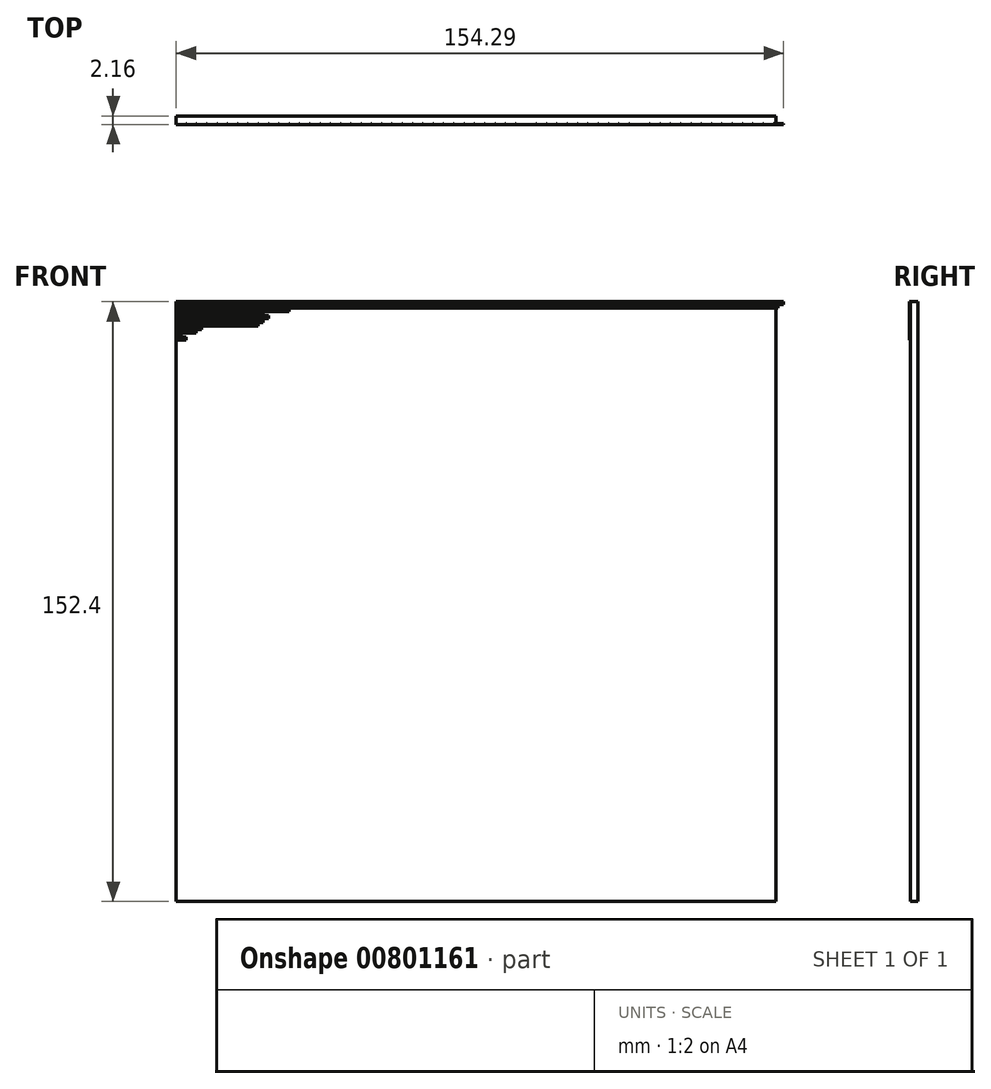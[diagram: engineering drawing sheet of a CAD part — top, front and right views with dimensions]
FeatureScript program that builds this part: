
annotation { "Feature Type Name" : "Feature", "Feature Type Description" : "" }
export const myFeature = defineFeature(function(context is Context, id is Id, definition is map)
    precondition{}
    {
        {
            var Q0;
            Q0=qCreatedBy(makeId("Front.planeOp"),FACE);
            var sketch = newSketch(context, id + "F0", { "sketchPlane" : qUnion([Q0])});
            skLineSegment(sketch, "E0.bottom", {"start": v(-76.2, -76.2) * mm, "end": v(76.2, -76.2) * mm});
            skLineSegment(sketch, "E0.top", {"start": v(-76.2, 76.2) * mm, "end": v(76.2, 76.2) * mm});
            skLineSegment(sketch, "E0.left", {"start": v(-76.2, -76.2) * mm, "end": v(-76.2, 76.2) * mm});
            skLineSegment(sketch, "E0.right", {"start": v(76.2, -76.2) * mm, "end": v(76.2, 76.2) * mm});
            skPoint(sketch, "E0.middle", {"position": v(0, 0) * mm});
            skSolve(sketch);
        }
        {
            var Q0;
            Q0 = qSketchRegion(id + "F0", true);
            extrude(context, id + "F1", {"entities" : qUnion([Q0]), "depth" : 1.9 * mm, "offsetDistance" : 25.4 * mm});
        }
        {
            var Q0;
            Q0=makeQuery(id+"F1.opExtrude","CAP_FACE",FACE,{"disambiguationData":[OSD([sQuery(id+"F0.wireOp",EDGE,"E0.bottom"),sQuery(id+"F0.wireOp",EDGE,"E0.top"),sQuery(id+"F0.wireOp",EDGE,"E0.left"),sQuery(id+"F0.wireOp",EDGE,"E0.right")])],"isStart":false});
            var sketch = newSketch(context, id + "F2", { "sketchPlane" : qUnion([Q0])});
            skLineSegment(sketch, "E1.bottom", {"start": v(-76.2, 76.2) * mm, "end": v(-73.71, 76.2) * mm});
            skLineSegment(sketch, "E1.top", {"start": v(-76.2, 75.44) * mm, "end": v(-73.71, 75.44) * mm});
            skLineSegment(sketch, "E1.left", {"start": v(-76.2, 76.2) * mm, "end": v(-76.2, 75.44) * mm});
            skLineSegment(sketch, "E1.right", {"start": v(-73.71, 76.2) * mm, "end": v(-73.71, 75.44) * mm});
            skLineSegment(sketch, "E2.bottom", {"start": v(-73.58, 76.2) * mm, "end": v(-71.1, 76.2) * mm});
            skLineSegment(sketch, "E2.top", {"start": v(-73.58, 75.44) * mm, "end": v(-71.1, 75.44) * mm});
            skLineSegment(sketch, "E2.left", {"start": v(-73.58, 76.2) * mm, "end": v(-73.58, 75.44) * mm});
            skLineSegment(sketch, "E2.right", {"start": v(-71.1, 76.2) * mm, "end": v(-71.1, 75.44) * mm});
            skLineSegment(sketch, "E3.bottom", {"start": v(-70.99, 76.2) * mm, "end": v(-68.49, 76.2) * mm});
            skLineSegment(sketch, "E3.top", {"start": v(-70.99, 75.44) * mm, "end": v(-68.49, 75.44) * mm});
            skLineSegment(sketch, "E3.left", {"start": v(-70.99, 76.2) * mm, "end": v(-70.99, 75.44) * mm});
            skLineSegment(sketch, "E3.right", {"start": v(-68.49, 76.2) * mm, "end": v(-68.49, 75.44) * mm});
            skLineSegment(sketch, "E4.bottom", {"start": v(-68.35, 76.2) * mm, "end": v(-65.86, 76.2) * mm});
            skLineSegment(sketch, "E4.top", {"start": v(-68.35, 75.44) * mm, "end": v(-65.86, 75.44) * mm});
            skLineSegment(sketch, "E4.left", {"start": v(-68.35, 76.2) * mm, "end": v(-68.35, 75.44) * mm});
            skLineSegment(sketch, "E4.right", {"start": v(-65.86, 76.2) * mm, "end": v(-65.86, 75.44) * mm});
            skLineSegment(sketch, "E5.bottom", {"start": v(-65.72, 76.2) * mm, "end": v(-63.23, 76.2) * mm});
            skLineSegment(sketch, "E5.top", {"start": v(-65.72, 75.44) * mm, "end": v(-63.23, 75.44) * mm});
            skLineSegment(sketch, "E5.left", {"start": v(-65.72, 76.2) * mm, "end": v(-65.72, 75.44) * mm});
            skLineSegment(sketch, "E5.right", {"start": v(-63.23, 76.2) * mm, "end": v(-63.23, 75.44) * mm});
            skLineSegment(sketch, "E6.bottom", {"start": v(-63.1, 76.2) * mm, "end": v(-60.62, 76.2) * mm});
            skLineSegment(sketch, "E6.top", {"start": v(-63.1, 75.44) * mm, "end": v(-60.62, 75.44) * mm});
            skLineSegment(sketch, "E6.left", {"start": v(-63.1, 76.2) * mm, "end": v(-63.1, 75.44) * mm});
            skLineSegment(sketch, "E6.right", {"start": v(-60.62, 76.2) * mm, "end": v(-60.62, 75.44) * mm});
            skLineSegment(sketch, "E7.bottom", {"start": v(-60.5, 76.2) * mm, "end": v(-58.02, 76.2) * mm});
            skLineSegment(sketch, "E7.top", {"start": v(-60.5, 75.44) * mm, "end": v(-58.02, 75.44) * mm});
            skLineSegment(sketch, "E7.left", {"start": v(-60.5, 76.2) * mm, "end": v(-60.5, 75.44) * mm});
            skLineSegment(sketch, "E7.right", {"start": v(-58.02, 76.2) * mm, "end": v(-58.02, 75.44) * mm});
            skLineSegment(sketch, "E8.bottom", {"start": v(-57.9, 76.2) * mm, "end": v(-55.4, 76.2) * mm});
            skLineSegment(sketch, "E8.top", {"start": v(-57.9, 75.44) * mm, "end": v(-55.4, 75.44) * mm});
            skLineSegment(sketch, "E8.left", {"start": v(-57.9, 76.2) * mm, "end": v(-57.9, 75.44) * mm});
            skLineSegment(sketch, "E8.right", {"start": v(-55.4, 76.2) * mm, "end": v(-55.4, 75.44) * mm});
            skLineSegment(sketch, "E9.bottom", {"start": v(-55.27, 76.2) * mm, "end": v(-52.78, 76.2) * mm});
            skLineSegment(sketch, "E9.top", {"start": v(-55.27, 75.44) * mm, "end": v(-52.78, 75.44) * mm});
            skLineSegment(sketch, "E9.left", {"start": v(-55.27, 76.2) * mm, "end": v(-55.27, 75.44) * mm});
            skLineSegment(sketch, "E9.right", {"start": v(-52.78, 76.2) * mm, "end": v(-52.78, 75.44) * mm});
            skPoint(sketch, "E10.oppositeSnap0", {"position": v(-74.96, 75.44) * mm});
            skLineSegment(sketch, "E10.bottom", {"start": v(-76.2, 75.44) * mm, "end": v(-74.96, 75.44) * mm});
            skLineSegment(sketch, "E10.left", {"start": v(-76.2, 75.44) * mm, "end": v(-76.2, 75.32) * mm});
            skLineSegment(sketch, "E11.bottom", {"start": v(-76.2, 75.32) * mm, "end": v(-75.01, 75.32) * mm});
            skLineSegment(sketch, "E11.top", {"start": v(-76.2, 74.56) * mm, "end": v(-75.01, 74.56) * mm});
            skLineSegment(sketch, "E11.left", {"start": v(-76.2, 75.32) * mm, "end": v(-76.2, 74.56) * mm});
            skLineSegment(sketch, "E11.right", {"start": v(-75.01, 75.32) * mm, "end": v(-75.01, 74.56) * mm});
            skLineSegment(sketch, "E12.bottom", {"start": v(-74.88, 75.32) * mm, "end": v(-72.38, 75.32) * mm});
            skLineSegment(sketch, "E12.top", {"start": v(-74.88, 74.56) * mm, "end": v(-72.38, 74.56) * mm});
            skLineSegment(sketch, "E12.left", {"start": v(-74.88, 75.32) * mm, "end": v(-74.88, 74.56) * mm});
            skLineSegment(sketch, "E12.right", {"start": v(-72.38, 75.32) * mm, "end": v(-72.38, 74.56) * mm});
            skLineSegment(sketch, "E13.bottom", {"start": v(-72.26, 75.32) * mm, "end": v(-69.76, 75.32) * mm});
            skLineSegment(sketch, "E13.top", {"start": v(-72.26, 74.56) * mm, "end": v(-69.76, 74.56) * mm});
            skLineSegment(sketch, "E13.left", {"start": v(-72.26, 75.32) * mm, "end": v(-72.26, 74.56) * mm});
            skLineSegment(sketch, "E13.right", {"start": v(-69.76, 75.32) * mm, "end": v(-69.76, 74.56) * mm});
            skLineSegment(sketch, "E14.bottom", {"start": v(-69.65, 75.32) * mm, "end": v(-67.16, 75.32) * mm});
            skLineSegment(sketch, "E14.top", {"start": v(-69.65, 74.56) * mm, "end": v(-67.16, 74.56) * mm});
            skLineSegment(sketch, "E14.left", {"start": v(-69.65, 75.32) * mm, "end": v(-69.65, 74.56) * mm});
            skLineSegment(sketch, "E14.right", {"start": v(-67.16, 75.32) * mm, "end": v(-67.16, 74.56) * mm});
            skLineSegment(sketch, "E15.bottom", {"start": v(-67.04, 75.32) * mm, "end": v(-64.55, 75.32) * mm});
            skLineSegment(sketch, "E15.top", {"start": v(-67.04, 74.56) * mm, "end": v(-64.55, 74.56) * mm});
            skLineSegment(sketch, "E15.left", {"start": v(-67.04, 75.32) * mm, "end": v(-67.04, 74.56) * mm});
            skLineSegment(sketch, "E15.right", {"start": v(-64.55, 75.32) * mm, "end": v(-64.55, 74.56) * mm});
            skLineSegment(sketch, "E16.bottom", {"start": v(-64.42, 75.32) * mm, "end": v(-61.95, 75.32) * mm});
            skLineSegment(sketch, "E16.top", {"start": v(-64.42, 74.56) * mm, "end": v(-61.95, 74.56) * mm});
            skLineSegment(sketch, "E16.left", {"start": v(-64.42, 75.32) * mm, "end": v(-64.42, 74.56) * mm});
            skLineSegment(sketch, "E16.right", {"start": v(-61.95, 75.32) * mm, "end": v(-61.95, 74.56) * mm});
            skLineSegment(sketch, "E17.bottom", {"start": v(-61.83, 75.32) * mm, "end": v(-59.35, 75.32) * mm});
            skLineSegment(sketch, "E17.top", {"start": v(-61.83, 74.56) * mm, "end": v(-59.35, 74.56) * mm});
            skLineSegment(sketch, "E17.left", {"start": v(-61.83, 75.32) * mm, "end": v(-61.83, 74.56) * mm});
            skLineSegment(sketch, "E17.right", {"start": v(-59.35, 75.32) * mm, "end": v(-59.35, 74.56) * mm});
            skLineSegment(sketch, "E18.bottom", {"start": v(-59.22, 75.32) * mm, "end": v(-56.74, 75.32) * mm});
            skLineSegment(sketch, "E18.top", {"start": v(-59.22, 74.56) * mm, "end": v(-56.74, 74.56) * mm});
            skLineSegment(sketch, "E18.left", {"start": v(-59.22, 75.32) * mm, "end": v(-59.22, 74.56) * mm});
            skLineSegment(sketch, "E18.right", {"start": v(-56.74, 75.32) * mm, "end": v(-56.74, 74.56) * mm});
            skLineSegment(sketch, "E19.bottom", {"start": v(-56.61, 75.32) * mm, "end": v(-54.13, 75.32) * mm});
            skLineSegment(sketch, "E19.top", {"start": v(-56.61, 74.56) * mm, "end": v(-54.13, 74.56) * mm});
            skLineSegment(sketch, "E19.left", {"start": v(-56.61, 75.32) * mm, "end": v(-56.61, 74.56) * mm});
            skLineSegment(sketch, "E19.right", {"start": v(-54.13, 75.32) * mm, "end": v(-54.13, 74.56) * mm});
            skLineSegment(sketch, "E20.bottom", {"start": v(-76.2, 74.43) * mm, "end": v(-73.71, 74.43) * mm});
            skLineSegment(sketch, "E20.top", {"start": v(-76.2, 73.65) * mm, "end": v(-73.71, 73.65) * mm});
            skLineSegment(sketch, "E20.left", {"start": v(-76.2, 74.43) * mm, "end": v(-76.2, 73.65) * mm});
            skLineSegment(sketch, "E20.right", {"start": v(-73.71, 74.43) * mm, "end": v(-73.71, 73.65) * mm});
            skLineSegment(sketch, "E21.bottom", {"start": v(-73.58, 74.43) * mm, "end": v(-71.1, 74.43) * mm});
            skLineSegment(sketch, "E21.top", {"start": v(-73.58, 73.65) * mm, "end": v(-71.1, 73.65) * mm});
            skLineSegment(sketch, "E21.left", {"start": v(-73.58, 74.43) * mm, "end": v(-73.58, 73.65) * mm});
            skLineSegment(sketch, "E21.right", {"start": v(-71.1, 74.43) * mm, "end": v(-71.1, 73.65) * mm});
            skLineSegment(sketch, "E22.bottom", {"start": v(-70.99, 74.43) * mm, "end": v(-68.49, 74.43) * mm});
            skLineSegment(sketch, "E22.top", {"start": v(-70.99, 73.65) * mm, "end": v(-68.49, 73.65) * mm});
            skLineSegment(sketch, "E22.left", {"start": v(-70.99, 74.43) * mm, "end": v(-70.99, 73.65) * mm});
            skLineSegment(sketch, "E22.right", {"start": v(-68.49, 74.43) * mm, "end": v(-68.49, 73.65) * mm});
            skLineSegment(sketch, "E23.bottom", {"start": v(-68.35, 74.43) * mm, "end": v(-65.86, 74.43) * mm});
            skLineSegment(sketch, "E23.top", {"start": v(-68.35, 73.65) * mm, "end": v(-65.86, 73.65) * mm});
            skLineSegment(sketch, "E23.left", {"start": v(-68.35, 74.43) * mm, "end": v(-68.35, 73.65) * mm});
            skLineSegment(sketch, "E23.right", {"start": v(-65.86, 74.43) * mm, "end": v(-65.86, 73.65) * mm});
            skLineSegment(sketch, "E24.bottom", {"start": v(-52.66, 76.2) * mm, "end": v(-50.18, 76.2) * mm});
            skLineSegment(sketch, "E24.top", {"start": v(-52.66, 75.44) * mm, "end": v(-50.18, 75.44) * mm});
            skLineSegment(sketch, "E24.left", {"start": v(-52.66, 76.2) * mm, "end": v(-52.66, 75.44) * mm});
            skLineSegment(sketch, "E24.right", {"start": v(-50.18, 76.2) * mm, "end": v(-50.18, 75.44) * mm});
            skLineSegment(sketch, "E25.bottom", {"start": v(-50.06, 76.2) * mm, "end": v(-47.57, 76.2) * mm});
            skLineSegment(sketch, "E25.top", {"start": v(-50.06, 75.44) * mm, "end": v(-47.57, 75.44) * mm});
            skLineSegment(sketch, "E25.left", {"start": v(-50.06, 76.2) * mm, "end": v(-50.06, 75.44) * mm});
            skLineSegment(sketch, "E25.right", {"start": v(-47.57, 76.2) * mm, "end": v(-47.57, 75.44) * mm});
            skLineSegment(sketch, "E26.bottom", {"start": v(-47.45, 76.2) * mm, "end": v(-44.95, 76.2) * mm});
            skLineSegment(sketch, "E26.top", {"start": v(-47.45, 75.44) * mm, "end": v(-44.95, 75.44) * mm});
            skLineSegment(sketch, "E26.left", {"start": v(-47.45, 76.2) * mm, "end": v(-47.45, 75.44) * mm});
            skLineSegment(sketch, "E26.right", {"start": v(-44.95, 76.2) * mm, "end": v(-44.95, 75.44) * mm});
            skLineSegment(sketch, "E27.bottom", {"start": v(-44.83, 76.2) * mm, "end": v(-42.34, 76.2) * mm});
            skLineSegment(sketch, "E27.top", {"start": v(-44.83, 75.44) * mm, "end": v(-42.34, 75.44) * mm});
            skLineSegment(sketch, "E27.left", {"start": v(-44.83, 76.2) * mm, "end": v(-44.83, 75.44) * mm});
            skLineSegment(sketch, "E27.right", {"start": v(-42.34, 76.2) * mm, "end": v(-42.34, 75.44) * mm});
            skLineSegment(sketch, "E28.bottom", {"start": v(-42.21, 76.2) * mm, "end": v(-39.72, 76.2) * mm});
            skLineSegment(sketch, "E28.top", {"start": v(-42.21, 75.44) * mm, "end": v(-39.72, 75.44) * mm});
            skLineSegment(sketch, "E28.left", {"start": v(-42.21, 76.2) * mm, "end": v(-42.21, 75.44) * mm});
            skLineSegment(sketch, "E28.right", {"start": v(-39.72, 76.2) * mm, "end": v(-39.72, 75.44) * mm});
            skLineSegment(sketch, "E29.bottom", {"start": v(-39.6, 76.2) * mm, "end": v(-37.1, 76.2) * mm});
            skLineSegment(sketch, "E29.top", {"start": v(-39.6, 75.44) * mm, "end": v(-37.1, 75.44) * mm});
            skLineSegment(sketch, "E29.left", {"start": v(-39.6, 76.2) * mm, "end": v(-39.6, 75.44) * mm});
            skLineSegment(sketch, "E29.right", {"start": v(-37.1, 76.2) * mm, "end": v(-37.1, 75.44) * mm});
            skLineSegment(sketch, "E30.bottom", {"start": v(-36.98, 76.2) * mm, "end": v(-34.5, 76.2) * mm});
            skLineSegment(sketch, "E30.top", {"start": v(-36.98, 75.44) * mm, "end": v(-34.5, 75.44) * mm});
            skLineSegment(sketch, "E30.left", {"start": v(-36.98, 76.2) * mm, "end": v(-36.98, 75.44) * mm});
            skLineSegment(sketch, "E30.right", {"start": v(-34.5, 76.2) * mm, "end": v(-34.5, 75.44) * mm});
            skLineSegment(sketch, "E31.bottom", {"start": v(-34.38, 76.2) * mm, "end": v(-31.9, 76.2) * mm});
            skLineSegment(sketch, "E31.top", {"start": v(-34.38, 75.44) * mm, "end": v(-31.9, 75.44) * mm});
            skLineSegment(sketch, "E31.left", {"start": v(-34.38, 76.2) * mm, "end": v(-34.38, 75.44) * mm});
            skLineSegment(sketch, "E31.right", {"start": v(-31.9, 76.2) * mm, "end": v(-31.9, 75.44) * mm});
            skLineSegment(sketch, "E32.bottom", {"start": v(-31.77, 76.2) * mm, "end": v(-29.29, 76.2) * mm});
            skLineSegment(sketch, "E32.top", {"start": v(-31.77, 75.44) * mm, "end": v(-29.29, 75.44) * mm});
            skLineSegment(sketch, "E32.left", {"start": v(-31.77, 76.2) * mm, "end": v(-31.77, 75.44) * mm});
            skLineSegment(sketch, "E32.right", {"start": v(-29.29, 76.2) * mm, "end": v(-29.29, 75.44) * mm});
            skLineSegment(sketch, "E33.bottom", {"start": v(-29.16, 76.2) * mm, "end": v(-26.66, 76.2) * mm});
            skLineSegment(sketch, "E33.top", {"start": v(-29.16, 75.44) * mm, "end": v(-26.66, 75.44) * mm});
            skLineSegment(sketch, "E33.left", {"start": v(-29.16, 76.2) * mm, "end": v(-29.16, 75.44) * mm});
            skLineSegment(sketch, "E33.right", {"start": v(-26.66, 76.2) * mm, "end": v(-26.66, 75.44) * mm});
            skLineSegment(sketch, "E34.bottom", {"start": v(-26.55, 76.2) * mm, "end": v(-24.06, 76.2) * mm});
            skLineSegment(sketch, "E34.top", {"start": v(-26.55, 75.44) * mm, "end": v(-24.06, 75.44) * mm});
            skLineSegment(sketch, "E34.left", {"start": v(-26.55, 76.2) * mm, "end": v(-26.55, 75.44) * mm});
            skLineSegment(sketch, "E34.right", {"start": v(-24.06, 76.2) * mm, "end": v(-24.06, 75.44) * mm});
            skLineSegment(sketch, "E35.bottom", {"start": v(-23.92, 76.2) * mm, "end": v(-21.44, 76.2) * mm});
            skLineSegment(sketch, "E35.top", {"start": v(-23.92, 75.44) * mm, "end": v(-21.44, 75.44) * mm});
            skLineSegment(sketch, "E35.left", {"start": v(-23.92, 76.2) * mm, "end": v(-23.92, 75.44) * mm});
            skLineSegment(sketch, "E35.right", {"start": v(-21.44, 76.2) * mm, "end": v(-21.44, 75.44) * mm});
            skLineSegment(sketch, "E36.bottom", {"start": v(-21.32, 76.2) * mm, "end": v(-18.84, 76.2) * mm});
            skLineSegment(sketch, "E36.top", {"start": v(-21.32, 75.44) * mm, "end": v(-18.84, 75.44) * mm});
            skLineSegment(sketch, "E36.left", {"start": v(-21.32, 76.2) * mm, "end": v(-21.32, 75.44) * mm});
            skLineSegment(sketch, "E36.right", {"start": v(-18.84, 76.2) * mm, "end": v(-18.84, 75.44) * mm});
            skLineSegment(sketch, "E37.bottom", {"start": v(-18.72, 76.2) * mm, "end": v(-16.21, 76.2) * mm});
            skLineSegment(sketch, "E37.top", {"start": v(-18.72, 75.44) * mm, "end": v(-16.21, 75.44) * mm});
            skLineSegment(sketch, "E37.left", {"start": v(-18.72, 76.2) * mm, "end": v(-18.72, 75.44) * mm});
            skLineSegment(sketch, "E37.right", {"start": v(-16.21, 76.2) * mm, "end": v(-16.21, 75.44) * mm});
            skLineSegment(sketch, "E38.bottom", {"start": v(-16.1, 76.2) * mm, "end": v(-13.6, 76.2) * mm});
            skLineSegment(sketch, "E38.top", {"start": v(-16.1, 75.44) * mm, "end": v(-13.6, 75.44) * mm});
            skLineSegment(sketch, "E38.left", {"start": v(-16.1, 76.2) * mm, "end": v(-16.1, 75.44) * mm});
            skLineSegment(sketch, "E38.right", {"start": v(-13.6, 76.2) * mm, "end": v(-13.6, 75.44) * mm});
            skLineSegment(sketch, "E39.bottom", {"start": v(-13.48, 76.2) * mm, "end": v(-11, 76.2) * mm});
            skLineSegment(sketch, "E39.top", {"start": v(-13.48, 75.44) * mm, "end": v(-11, 75.44) * mm});
            skLineSegment(sketch, "E39.left", {"start": v(-13.48, 76.2) * mm, "end": v(-13.48, 75.44) * mm});
            skLineSegment(sketch, "E39.right", {"start": v(-11, 76.2) * mm, "end": v(-11, 75.44) * mm});
            skLineSegment(sketch, "E40.bottom", {"start": v(-10.87, 76.2) * mm, "end": v(-8.38, 76.2) * mm});
            skLineSegment(sketch, "E40.top", {"start": v(-10.87, 75.44) * mm, "end": v(-8.38, 75.44) * mm});
            skLineSegment(sketch, "E40.left", {"start": v(-10.87, 76.2) * mm, "end": v(-10.87, 75.44) * mm});
            skLineSegment(sketch, "E40.right", {"start": v(-8.38, 76.2) * mm, "end": v(-8.38, 75.44) * mm});
            skLineSegment(sketch, "E41.bottom", {"start": v(-8.24, 76.2) * mm, "end": v(-5.76, 76.2) * mm});
            skLineSegment(sketch, "E41.top", {"start": v(-8.24, 75.44) * mm, "end": v(-5.76, 75.44) * mm});
            skLineSegment(sketch, "E41.left", {"start": v(-8.24, 76.2) * mm, "end": v(-8.24, 75.44) * mm});
            skLineSegment(sketch, "E41.right", {"start": v(-5.76, 76.2) * mm, "end": v(-5.76, 75.44) * mm});
            skLineSegment(sketch, "E42.bottom", {"start": v(-5.63, 76.2) * mm, "end": v(-3.13, 76.2) * mm});
            skLineSegment(sketch, "E42.top", {"start": v(-5.63, 75.44) * mm, "end": v(-3.13, 75.44) * mm});
            skLineSegment(sketch, "E42.left", {"start": v(-5.63, 76.2) * mm, "end": v(-5.63, 75.44) * mm});
            skLineSegment(sketch, "E42.right", {"start": v(-3.13, 76.2) * mm, "end": v(-3.13, 75.44) * mm});
            skLineSegment(sketch, "E43.bottom", {"start": v(-3, 76.2) * mm, "end": v(-0.53, 76.2) * mm});
            skLineSegment(sketch, "E43.top", {"start": v(-3, 75.44) * mm, "end": v(-0.53, 75.44) * mm});
            skLineSegment(sketch, "E43.left", {"start": v(-3, 76.2) * mm, "end": v(-3, 75.44) * mm});
            skLineSegment(sketch, "E43.right", {"start": v(-0.53, 76.2) * mm, "end": v(-0.53, 75.44) * mm});
            skLineSegment(sketch, "E44.bottom", {"start": v(-0.4, 76.2) * mm, "end": v(2.1, 76.2) * mm});
            skLineSegment(sketch, "E44.top", {"start": v(-0.4, 75.44) * mm, "end": v(2.1, 75.44) * mm});
            skLineSegment(sketch, "E44.left", {"start": v(-0.4, 76.2) * mm, "end": v(-0.4, 75.44) * mm});
            skLineSegment(sketch, "E44.right", {"start": v(2.1, 76.2) * mm, "end": v(2.1, 75.44) * mm});
            skLineSegment(sketch, "E45.bottom", {"start": v(2.23, 76.2) * mm, "end": v(4.73, 76.2) * mm});
            skLineSegment(sketch, "E45.top", {"start": v(2.23, 75.44) * mm, "end": v(4.73, 75.44) * mm});
            skLineSegment(sketch, "E45.left", {"start": v(2.23, 76.2) * mm, "end": v(2.23, 75.44) * mm});
            skLineSegment(sketch, "E45.right", {"start": v(4.73, 76.2) * mm, "end": v(4.73, 75.44) * mm});
            skLineSegment(sketch, "E46.bottom", {"start": v(4.87, 76.2) * mm, "end": v(7.37, 76.2) * mm});
            skLineSegment(sketch, "E46.top", {"start": v(4.87, 75.44) * mm, "end": v(7.37, 75.44) * mm});
            skLineSegment(sketch, "E46.left", {"start": v(4.87, 76.2) * mm, "end": v(4.87, 75.44) * mm});
            skLineSegment(sketch, "E46.right", {"start": v(7.37, 76.2) * mm, "end": v(7.37, 75.44) * mm});
            skLineSegment(sketch, "E47.bottom", {"start": v(7.5, 76.2) * mm, "end": v(9.99, 76.2) * mm});
            skLineSegment(sketch, "E47.top", {"start": v(7.5, 75.44) * mm, "end": v(9.99, 75.44) * mm});
            skLineSegment(sketch, "E47.left", {"start": v(7.5, 76.2) * mm, "end": v(7.5, 75.44) * mm});
            skLineSegment(sketch, "E47.right", {"start": v(9.99, 76.2) * mm, "end": v(9.99, 75.44) * mm});
            skLineSegment(sketch, "E48.bottom", {"start": v(10.1, 76.2) * mm, "end": v(12.6, 76.2) * mm});
            skLineSegment(sketch, "E48.top", {"start": v(10.1, 75.44) * mm, "end": v(12.6, 75.44) * mm});
            skLineSegment(sketch, "E48.left", {"start": v(10.1, 76.2) * mm, "end": v(10.1, 75.44) * mm});
            skLineSegment(sketch, "E48.right", {"start": v(12.6, 76.2) * mm, "end": v(12.6, 75.44) * mm});
            skLineSegment(sketch, "E49.bottom", {"start": v(12.72, 76.2) * mm, "end": v(15.22, 76.2) * mm});
            skLineSegment(sketch, "E49.top", {"start": v(12.72, 75.44) * mm, "end": v(15.22, 75.44) * mm});
            skLineSegment(sketch, "E49.left", {"start": v(12.72, 76.2) * mm, "end": v(12.72, 75.44) * mm});
            skLineSegment(sketch, "E49.right", {"start": v(15.22, 76.2) * mm, "end": v(15.22, 75.44) * mm});
            skLineSegment(sketch, "E50.bottom", {"start": v(15.35, 76.2) * mm, "end": v(17.84, 76.2) * mm});
            skLineSegment(sketch, "E50.top", {"start": v(15.35, 75.44) * mm, "end": v(17.84, 75.44) * mm});
            skLineSegment(sketch, "E50.left", {"start": v(15.35, 76.2) * mm, "end": v(15.35, 75.44) * mm});
            skLineSegment(sketch, "E50.right", {"start": v(17.84, 76.2) * mm, "end": v(17.84, 75.44) * mm});
            skLineSegment(sketch, "E51.bottom", {"start": v(17.97, 76.2) * mm, "end": v(20.46, 76.2) * mm});
            skLineSegment(sketch, "E51.top", {"start": v(17.97, 75.44) * mm, "end": v(20.46, 75.44) * mm});
            skLineSegment(sketch, "E51.left", {"start": v(17.97, 76.2) * mm, "end": v(17.97, 75.44) * mm});
            skLineSegment(sketch, "E51.right", {"start": v(20.46, 76.2) * mm, "end": v(20.46, 75.44) * mm});
            skLineSegment(sketch, "E52.bottom", {"start": v(20.6, 76.2) * mm, "end": v(23.07, 76.2) * mm});
            skLineSegment(sketch, "E52.top", {"start": v(20.6, 75.44) * mm, "end": v(23.07, 75.44) * mm});
            skLineSegment(sketch, "E52.left", {"start": v(20.6, 76.2) * mm, "end": v(20.6, 75.44) * mm});
            skLineSegment(sketch, "E52.right", {"start": v(23.07, 76.2) * mm, "end": v(23.07, 75.44) * mm});
            skLineSegment(sketch, "E53.bottom", {"start": v(23.2, 76.2) * mm, "end": v(25.7, 76.2) * mm});
            skLineSegment(sketch, "E53.top", {"start": v(23.2, 75.44) * mm, "end": v(25.7, 75.44) * mm});
            skLineSegment(sketch, "E53.left", {"start": v(23.2, 76.2) * mm, "end": v(23.2, 75.44) * mm});
            skLineSegment(sketch, "E53.right", {"start": v(25.7, 76.2) * mm, "end": v(25.7, 75.44) * mm});
            skLineSegment(sketch, "E54.bottom", {"start": v(25.83, 76.2) * mm, "end": v(28.32, 76.2) * mm});
            skLineSegment(sketch, "E54.top", {"start": v(25.83, 75.44) * mm, "end": v(28.32, 75.44) * mm});
            skLineSegment(sketch, "E54.left", {"start": v(25.83, 76.2) * mm, "end": v(25.83, 75.44) * mm});
            skLineSegment(sketch, "E54.right", {"start": v(28.32, 76.2) * mm, "end": v(28.32, 75.44) * mm});
            skLineSegment(sketch, "E55.bottom", {"start": v(28.45, 76.2) * mm, "end": v(30.93, 76.2) * mm});
            skLineSegment(sketch, "E55.top", {"start": v(28.45, 75.44) * mm, "end": v(30.93, 75.44) * mm});
            skLineSegment(sketch, "E55.left", {"start": v(28.45, 76.2) * mm, "end": v(28.45, 75.44) * mm});
            skLineSegment(sketch, "E55.right", {"start": v(30.93, 76.2) * mm, "end": v(30.93, 75.44) * mm});
            skLineSegment(sketch, "E56.bottom", {"start": v(31.06, 76.2) * mm, "end": v(33.55, 76.2) * mm});
            skLineSegment(sketch, "E56.top", {"start": v(31.06, 75.44) * mm, "end": v(33.55, 75.44) * mm});
            skLineSegment(sketch, "E56.left", {"start": v(31.06, 76.2) * mm, "end": v(31.06, 75.44) * mm});
            skLineSegment(sketch, "E56.right", {"start": v(33.55, 76.2) * mm, "end": v(33.55, 75.44) * mm});
            skLineSegment(sketch, "E57.bottom", {"start": v(33.69, 76.2) * mm, "end": v(36.19, 76.2) * mm});
            skLineSegment(sketch, "E57.top", {"start": v(33.69, 75.44) * mm, "end": v(36.19, 75.44) * mm});
            skLineSegment(sketch, "E57.left", {"start": v(33.69, 76.2) * mm, "end": v(33.69, 75.44) * mm});
            skLineSegment(sketch, "E57.right", {"start": v(36.19, 76.2) * mm, "end": v(36.19, 75.44) * mm});
            skLineSegment(sketch, "E58.bottom", {"start": v(36.31, 76.2) * mm, "end": v(38.81, 76.2) * mm});
            skLineSegment(sketch, "E58.top", {"start": v(36.31, 75.44) * mm, "end": v(38.81, 75.44) * mm});
            skLineSegment(sketch, "E58.left", {"start": v(36.31, 76.2) * mm, "end": v(36.31, 75.44) * mm});
            skLineSegment(sketch, "E58.right", {"start": v(38.81, 76.2) * mm, "end": v(38.81, 75.44) * mm});
            skLineSegment(sketch, "E59.bottom", {"start": v(38.94, 76.2) * mm, "end": v(41.43, 76.2) * mm});
            skLineSegment(sketch, "E59.top", {"start": v(38.94, 75.44) * mm, "end": v(41.43, 75.44) * mm});
            skLineSegment(sketch, "E59.left", {"start": v(38.94, 76.2) * mm, "end": v(38.94, 75.44) * mm});
            skLineSegment(sketch, "E59.right", {"start": v(41.43, 76.2) * mm, "end": v(41.43, 75.44) * mm});
            skLineSegment(sketch, "E60.bottom", {"start": v(41.54, 76.2) * mm, "end": v(44.04, 76.2) * mm});
            skLineSegment(sketch, "E60.top", {"start": v(41.54, 75.44) * mm, "end": v(44.04, 75.44) * mm});
            skLineSegment(sketch, "E60.left", {"start": v(41.54, 76.2) * mm, "end": v(41.54, 75.44) * mm});
            skLineSegment(sketch, "E60.right", {"start": v(44.04, 76.2) * mm, "end": v(44.04, 75.44) * mm});
            skLineSegment(sketch, "E61.bottom", {"start": v(44.16, 76.2) * mm, "end": v(46.66, 76.2) * mm});
            skLineSegment(sketch, "E61.top", {"start": v(44.16, 75.44) * mm, "end": v(46.66, 75.44) * mm});
            skLineSegment(sketch, "E61.left", {"start": v(44.16, 76.2) * mm, "end": v(44.16, 75.44) * mm});
            skLineSegment(sketch, "E61.right", {"start": v(46.66, 76.2) * mm, "end": v(46.66, 75.44) * mm});
            skLineSegment(sketch, "E62.bottom", {"start": v(46.78, 76.2) * mm, "end": v(49.28, 76.2) * mm});
            skLineSegment(sketch, "E62.top", {"start": v(46.78, 75.44) * mm, "end": v(49.28, 75.44) * mm});
            skLineSegment(sketch, "E62.left", {"start": v(46.78, 76.2) * mm, "end": v(46.78, 75.44) * mm});
            skLineSegment(sketch, "E62.right", {"start": v(49.28, 76.2) * mm, "end": v(49.28, 75.44) * mm});
            skLineSegment(sketch, "E63.bottom", {"start": v(49.4, 76.2) * mm, "end": v(51.9, 76.2) * mm});
            skLineSegment(sketch, "E63.top", {"start": v(49.4, 75.44) * mm, "end": v(51.9, 75.44) * mm});
            skLineSegment(sketch, "E63.left", {"start": v(49.4, 76.2) * mm, "end": v(49.4, 75.44) * mm});
            skLineSegment(sketch, "E63.right", {"start": v(51.9, 76.2) * mm, "end": v(51.9, 75.44) * mm});
            skLineSegment(sketch, "E64.bottom", {"start": v(52.03, 76.2) * mm, "end": v(54.51, 76.2) * mm});
            skLineSegment(sketch, "E64.top", {"start": v(52.03, 75.44) * mm, "end": v(54.51, 75.44) * mm});
            skLineSegment(sketch, "E64.left", {"start": v(52.03, 76.2) * mm, "end": v(52.03, 75.44) * mm});
            skLineSegment(sketch, "E64.right", {"start": v(54.51, 76.2) * mm, "end": v(54.51, 75.44) * mm});
            skLineSegment(sketch, "E65.bottom", {"start": v(54.63, 76.2) * mm, "end": v(57.11, 76.2) * mm});
            skLineSegment(sketch, "E65.top", {"start": v(54.63, 75.44) * mm, "end": v(57.11, 75.44) * mm});
            skLineSegment(sketch, "E65.left", {"start": v(54.63, 76.2) * mm, "end": v(54.63, 75.44) * mm});
            skLineSegment(sketch, "E65.right", {"start": v(57.11, 76.2) * mm, "end": v(57.11, 75.44) * mm});
            skLineSegment(sketch, "E66.bottom", {"start": v(57.25, 76.2) * mm, "end": v(59.74, 76.2) * mm});
            skLineSegment(sketch, "E66.top", {"start": v(57.25, 75.44) * mm, "end": v(59.74, 75.44) * mm});
            skLineSegment(sketch, "E66.left", {"start": v(57.25, 76.2) * mm, "end": v(57.25, 75.44) * mm});
            skLineSegment(sketch, "E66.right", {"start": v(59.74, 76.2) * mm, "end": v(59.74, 75.44) * mm});
            skLineSegment(sketch, "E67.bottom", {"start": v(59.87, 76.2) * mm, "end": v(62.37, 76.2) * mm});
            skLineSegment(sketch, "E67.top", {"start": v(59.87, 75.44) * mm, "end": v(62.37, 75.44) * mm});
            skLineSegment(sketch, "E67.left", {"start": v(59.87, 76.2) * mm, "end": v(59.87, 75.44) * mm});
            skLineSegment(sketch, "E67.right", {"start": v(62.37, 76.2) * mm, "end": v(62.37, 75.44) * mm});
            skLineSegment(sketch, "E68.bottom", {"start": v(62.5, 76.2) * mm, "end": v(65, 76.2) * mm});
            skLineSegment(sketch, "E68.top", {"start": v(62.5, 75.44) * mm, "end": v(65, 75.44) * mm});
            skLineSegment(sketch, "E68.left", {"start": v(62.5, 76.2) * mm, "end": v(62.5, 75.44) * mm});
            skLineSegment(sketch, "E68.right", {"start": v(65, 76.2) * mm, "end": v(65, 75.44) * mm});
            skLineSegment(sketch, "E69.bottom", {"start": v(65.13, 76.2) * mm, "end": v(67.62, 76.2) * mm});
            skLineSegment(sketch, "E69.top", {"start": v(65.13, 75.44) * mm, "end": v(67.62, 75.44) * mm});
            skLineSegment(sketch, "E69.left", {"start": v(65.13, 76.2) * mm, "end": v(65.13, 75.44) * mm});
            skLineSegment(sketch, "E69.right", {"start": v(67.62, 76.2) * mm, "end": v(67.62, 75.44) * mm});
            skLineSegment(sketch, "E70.bottom", {"start": v(67.75, 76.2) * mm, "end": v(70.25, 76.2) * mm});
            skLineSegment(sketch, "E70.top", {"start": v(67.75, 75.44) * mm, "end": v(70.25, 75.44) * mm});
            skLineSegment(sketch, "E70.left", {"start": v(67.75, 76.2) * mm, "end": v(67.75, 75.44) * mm});
            skLineSegment(sketch, "E70.right", {"start": v(70.25, 76.2) * mm, "end": v(70.25, 75.44) * mm});
            skLineSegment(sketch, "E71.bottom", {"start": v(70.38, 76.2) * mm, "end": v(72.86, 76.2) * mm});
            skLineSegment(sketch, "E71.top", {"start": v(70.38, 75.44) * mm, "end": v(72.86, 75.44) * mm});
            skLineSegment(sketch, "E71.left", {"start": v(70.38, 76.2) * mm, "end": v(70.38, 75.44) * mm});
            skLineSegment(sketch, "E71.right", {"start": v(72.86, 76.2) * mm, "end": v(72.86, 75.44) * mm});
            skLineSegment(sketch, "E72.bottom", {"start": v(73, 76.2) * mm, "end": v(75.48, 76.2) * mm});
            skLineSegment(sketch, "E72.top", {"start": v(73, 75.44) * mm, "end": v(75.48, 75.44) * mm});
            skLineSegment(sketch, "E72.left", {"start": v(73, 76.2) * mm, "end": v(73, 75.44) * mm});
            skLineSegment(sketch, "E72.right", {"start": v(75.48, 76.2) * mm, "end": v(75.48, 75.44) * mm});
            skLineSegment(sketch, "E73.bottom", {"start": v(75.6, 76.2) * mm, "end": v(78.1, 76.2) * mm});
            skLineSegment(sketch, "E73.top", {"start": v(75.6, 75.44) * mm, "end": v(78.1, 75.44) * mm});
            skLineSegment(sketch, "E73.left", {"start": v(75.6, 76.2) * mm, "end": v(75.6, 75.44) * mm});
            skLineSegment(sketch, "E73.right", {"start": v(78.1, 76.2) * mm, "end": v(78.1, 75.44) * mm});
            skLineSegment(sketch, "E74.bottom", {"start": v(-54, 75.32) * mm, "end": v(-51.5, 75.32) * mm});
            skLineSegment(sketch, "E74.top", {"start": v(-54, 74.56) * mm, "end": v(-51.5, 74.56) * mm});
            skLineSegment(sketch, "E74.left", {"start": v(-54, 75.32) * mm, "end": v(-54, 74.56) * mm});
            skLineSegment(sketch, "E74.right", {"start": v(-51.5, 75.32) * mm, "end": v(-51.5, 74.56) * mm});
            skLineSegment(sketch, "E75.bottom", {"start": v(-51.38, 75.32) * mm, "end": v(-48.88, 75.32) * mm});
            skLineSegment(sketch, "E75.top", {"start": v(-51.38, 74.56) * mm, "end": v(-48.88, 74.56) * mm});
            skLineSegment(sketch, "E75.left", {"start": v(-51.38, 75.32) * mm, "end": v(-51.38, 74.56) * mm});
            skLineSegment(sketch, "E75.right", {"start": v(-48.88, 75.32) * mm, "end": v(-48.88, 74.56) * mm});
            skLineSegment(sketch, "E76.bottom", {"start": v(-48.75, 75.32) * mm, "end": v(-46.25, 75.32) * mm});
            skLineSegment(sketch, "E76.top", {"start": v(-48.75, 74.56) * mm, "end": v(-46.25, 74.56) * mm});
            skLineSegment(sketch, "E76.left", {"start": v(-48.75, 75.32) * mm, "end": v(-48.75, 74.56) * mm});
            skLineSegment(sketch, "E76.right", {"start": v(-46.25, 75.32) * mm, "end": v(-46.25, 74.56) * mm});
            skLineSegment(sketch, "E77.bottom", {"start": v(-46.13, 75.32) * mm, "end": v(-43.64, 75.32) * mm});
            skLineSegment(sketch, "E77.top", {"start": v(-46.13, 74.56) * mm, "end": v(-43.64, 74.56) * mm});
            skLineSegment(sketch, "E77.left", {"start": v(-46.13, 75.32) * mm, "end": v(-46.13, 74.56) * mm});
            skLineSegment(sketch, "E77.right", {"start": v(-43.64, 75.32) * mm, "end": v(-43.64, 74.56) * mm});
            skLineSegment(sketch, "E78.bottom", {"start": v(-43.52, 75.32) * mm, "end": v(-41.04, 75.32) * mm});
            skLineSegment(sketch, "E78.top", {"start": v(-43.52, 74.56) * mm, "end": v(-41.04, 74.56) * mm});
            skLineSegment(sketch, "E78.left", {"start": v(-43.52, 75.32) * mm, "end": v(-43.52, 74.56) * mm});
            skLineSegment(sketch, "E78.right", {"start": v(-41.04, 75.32) * mm, "end": v(-41.04, 74.56) * mm});
            skLineSegment(sketch, "E79.bottom", {"start": v(-40.92, 75.32) * mm, "end": v(-38.44, 75.32) * mm});
            skLineSegment(sketch, "E79.top", {"start": v(-40.92, 74.56) * mm, "end": v(-38.44, 74.56) * mm});
            skLineSegment(sketch, "E79.left", {"start": v(-40.92, 75.32) * mm, "end": v(-40.92, 74.56) * mm});
            skLineSegment(sketch, "E79.right", {"start": v(-38.44, 75.32) * mm, "end": v(-38.44, 74.56) * mm});
            skLineSegment(sketch, "E80.bottom", {"start": v(-38.3, 75.32) * mm, "end": v(-35.82, 75.32) * mm});
            skLineSegment(sketch, "E80.top", {"start": v(-38.3, 74.56) * mm, "end": v(-35.82, 74.56) * mm});
            skLineSegment(sketch, "E80.left", {"start": v(-38.3, 75.32) * mm, "end": v(-38.3, 74.56) * mm});
            skLineSegment(sketch, "E80.right", {"start": v(-35.82, 75.32) * mm, "end": v(-35.82, 74.56) * mm});
            skLineSegment(sketch, "E81.bottom", {"start": v(-35.7, 75.32) * mm, "end": v(-33.22, 75.32) * mm});
            skLineSegment(sketch, "E81.top", {"start": v(-35.7, 74.56) * mm, "end": v(-33.22, 74.56) * mm});
            skLineSegment(sketch, "E81.left", {"start": v(-35.7, 75.32) * mm, "end": v(-35.7, 74.56) * mm});
            skLineSegment(sketch, "E81.right", {"start": v(-33.22, 75.32) * mm, "end": v(-33.22, 74.56) * mm});
            skLineSegment(sketch, "E82.bottom", {"start": v(-33.1, 75.32) * mm, "end": v(-30.6, 75.32) * mm});
            skLineSegment(sketch, "E82.top", {"start": v(-33.1, 74.56) * mm, "end": v(-30.6, 74.56) * mm});
            skLineSegment(sketch, "E82.left", {"start": v(-33.1, 75.32) * mm, "end": v(-33.1, 74.56) * mm});
            skLineSegment(sketch, "E82.right", {"start": v(-30.6, 75.32) * mm, "end": v(-30.6, 74.56) * mm});
            skLineSegment(sketch, "E83.bottom", {"start": v(-30.47, 75.32) * mm, "end": v(-28, 75.32) * mm});
            skLineSegment(sketch, "E83.top", {"start": v(-30.47, 74.56) * mm, "end": v(-28, 74.56) * mm});
            skLineSegment(sketch, "E83.left", {"start": v(-30.47, 75.32) * mm, "end": v(-30.47, 74.56) * mm});
            skLineSegment(sketch, "E83.right", {"start": v(-28, 75.32) * mm, "end": v(-28, 74.56) * mm});
            skLineSegment(sketch, "E84.bottom", {"start": v(-27.86, 75.32) * mm, "end": v(-25.38, 75.32) * mm});
            skLineSegment(sketch, "E84.top", {"start": v(-27.86, 74.56) * mm, "end": v(-25.38, 74.56) * mm});
            skLineSegment(sketch, "E84.left", {"start": v(-27.86, 75.32) * mm, "end": v(-27.86, 74.56) * mm});
            skLineSegment(sketch, "E84.right", {"start": v(-25.38, 75.32) * mm, "end": v(-25.38, 74.56) * mm});
            skLineSegment(sketch, "E85.bottom", {"start": v(-25.26, 75.32) * mm, "end": v(-22.76, 75.32) * mm});
            skLineSegment(sketch, "E85.top", {"start": v(-25.26, 74.56) * mm, "end": v(-22.76, 74.56) * mm});
            skLineSegment(sketch, "E85.left", {"start": v(-25.26, 75.32) * mm, "end": v(-25.26, 74.56) * mm});
            skLineSegment(sketch, "E85.right", {"start": v(-22.76, 75.32) * mm, "end": v(-22.76, 74.56) * mm});
            skLineSegment(sketch, "E86.bottom", {"start": v(-22.63, 75.32) * mm, "end": v(-20.14, 75.32) * mm});
            skLineSegment(sketch, "E86.top", {"start": v(-22.63, 74.56) * mm, "end": v(-20.14, 74.56) * mm});
            skLineSegment(sketch, "E86.left", {"start": v(-22.63, 75.32) * mm, "end": v(-22.63, 74.56) * mm});
            skLineSegment(sketch, "E86.right", {"start": v(-20.14, 75.32) * mm, "end": v(-20.14, 74.56) * mm});
            skLineSegment(sketch, "E87.bottom", {"start": v(-20.02, 75.32) * mm, "end": v(-17.52, 75.32) * mm});
            skLineSegment(sketch, "E87.top", {"start": v(-20.02, 74.56) * mm, "end": v(-17.52, 74.56) * mm});
            skLineSegment(sketch, "E87.left", {"start": v(-20.02, 75.32) * mm, "end": v(-20.02, 74.56) * mm});
            skLineSegment(sketch, "E87.right", {"start": v(-17.52, 75.32) * mm, "end": v(-17.52, 74.56) * mm});
            skLineSegment(sketch, "E88.bottom", {"start": v(-17.39, 75.32) * mm, "end": v(-14.9, 75.32) * mm});
            skLineSegment(sketch, "E88.top", {"start": v(-17.39, 74.56) * mm, "end": v(-14.9, 74.56) * mm});
            skLineSegment(sketch, "E88.left", {"start": v(-17.39, 75.32) * mm, "end": v(-17.39, 74.56) * mm});
            skLineSegment(sketch, "E88.right", {"start": v(-14.9, 75.32) * mm, "end": v(-14.9, 74.56) * mm});
            skLineSegment(sketch, "E89.bottom", {"start": v(-14.77, 75.32) * mm, "end": v(-12.28, 75.32) * mm});
            skLineSegment(sketch, "E89.top", {"start": v(-14.77, 74.56) * mm, "end": v(-12.28, 74.56) * mm});
            skLineSegment(sketch, "E89.left", {"start": v(-14.77, 75.32) * mm, "end": v(-14.77, 74.56) * mm});
            skLineSegment(sketch, "E89.right", {"start": v(-12.28, 75.32) * mm, "end": v(-12.28, 74.56) * mm});
            skLineSegment(sketch, "E90.bottom", {"start": v(-12.15, 75.32) * mm, "end": v(-9.67, 75.32) * mm});
            skLineSegment(sketch, "E90.top", {"start": v(-12.15, 74.56) * mm, "end": v(-9.67, 74.56) * mm});
            skLineSegment(sketch, "E90.left", {"start": v(-12.15, 75.32) * mm, "end": v(-12.15, 74.56) * mm});
            skLineSegment(sketch, "E90.right", {"start": v(-9.67, 75.32) * mm, "end": v(-9.67, 74.56) * mm});
            skLineSegment(sketch, "E91.bottom", {"start": v(-9.53, 75.32) * mm, "end": v(-7.05, 75.32) * mm});
            skLineSegment(sketch, "E91.top", {"start": v(-9.53, 74.56) * mm, "end": v(-7.05, 74.56) * mm});
            skLineSegment(sketch, "E91.left", {"start": v(-9.53, 75.32) * mm, "end": v(-9.53, 74.56) * mm});
            skLineSegment(sketch, "E91.right", {"start": v(-7.05, 75.32) * mm, "end": v(-7.05, 74.56) * mm});
            skLineSegment(sketch, "E92.bottom", {"start": v(-6.92, 75.32) * mm, "end": v(-4.42, 75.32) * mm});
            skLineSegment(sketch, "E92.top", {"start": v(-6.92, 74.56) * mm, "end": v(-4.42, 74.56) * mm});
            skLineSegment(sketch, "E92.left", {"start": v(-6.92, 75.32) * mm, "end": v(-6.92, 74.56) * mm});
            skLineSegment(sketch, "E92.right", {"start": v(-4.42, 75.32) * mm, "end": v(-4.42, 74.56) * mm});
            skLineSegment(sketch, "E93.bottom", {"start": v(-4.3, 75.32) * mm, "end": v(-1.82, 75.32) * mm});
            skLineSegment(sketch, "E93.top", {"start": v(-4.3, 74.56) * mm, "end": v(-1.82, 74.56) * mm});
            skLineSegment(sketch, "E93.left", {"start": v(-4.3, 75.32) * mm, "end": v(-4.3, 74.56) * mm});
            skLineSegment(sketch, "E93.right", {"start": v(-1.82, 75.32) * mm, "end": v(-1.82, 74.56) * mm});
            skLineSegment(sketch, "E94.bottom", {"start": v(-1.69, 75.32) * mm, "end": v(0.8, 75.32) * mm});
            skLineSegment(sketch, "E94.top", {"start": v(-1.69, 74.56) * mm, "end": v(0.8, 74.56) * mm});
            skLineSegment(sketch, "E94.left", {"start": v(-1.69, 75.32) * mm, "end": v(-1.69, 74.56) * mm});
            skLineSegment(sketch, "E94.right", {"start": v(0.8, 75.32) * mm, "end": v(0.8, 74.56) * mm});
            skLineSegment(sketch, "E95.bottom", {"start": v(0.93, 75.32) * mm, "end": v(3.41, 75.32) * mm});
            skLineSegment(sketch, "E95.top", {"start": v(0.93, 74.56) * mm, "end": v(3.41, 74.56) * mm});
            skLineSegment(sketch, "E95.left", {"start": v(0.93, 75.32) * mm, "end": v(0.93, 74.56) * mm});
            skLineSegment(sketch, "E95.right", {"start": v(3.41, 75.32) * mm, "end": v(3.41, 74.56) * mm});
            skLineSegment(sketch, "E96.bottom", {"start": v(3.55, 75.32) * mm, "end": v(6.04, 75.32) * mm});
            skLineSegment(sketch, "E96.top", {"start": v(3.55, 74.56) * mm, "end": v(6.04, 74.56) * mm});
            skLineSegment(sketch, "E96.left", {"start": v(3.55, 75.32) * mm, "end": v(3.55, 74.56) * mm});
            skLineSegment(sketch, "E96.right", {"start": v(6.04, 75.32) * mm, "end": v(6.04, 74.56) * mm});
            skLineSegment(sketch, "E97.bottom", {"start": v(6.16, 75.32) * mm, "end": v(8.66, 75.32) * mm});
            skLineSegment(sketch, "E97.top", {"start": v(6.16, 74.56) * mm, "end": v(8.66, 74.56) * mm});
            skLineSegment(sketch, "E97.left", {"start": v(6.16, 75.32) * mm, "end": v(6.16, 74.56) * mm});
            skLineSegment(sketch, "E97.right", {"start": v(8.66, 75.32) * mm, "end": v(8.66, 74.56) * mm});
            skLineSegment(sketch, "E98.bottom", {"start": v(8.78, 75.32) * mm, "end": v(11.27, 75.32) * mm});
            skLineSegment(sketch, "E98.top", {"start": v(8.78, 74.56) * mm, "end": v(11.27, 74.56) * mm});
            skLineSegment(sketch, "E98.left", {"start": v(8.78, 75.32) * mm, "end": v(8.78, 74.56) * mm});
            skLineSegment(sketch, "E98.right", {"start": v(11.27, 75.32) * mm, "end": v(11.27, 74.56) * mm});
            skLineSegment(sketch, "E99.bottom", {"start": v(11.4, 75.32) * mm, "end": v(13.88, 75.32) * mm});
            skLineSegment(sketch, "E99.top", {"start": v(11.4, 74.56) * mm, "end": v(13.88, 74.56) * mm});
            skLineSegment(sketch, "E99.left", {"start": v(11.4, 75.32) * mm, "end": v(11.4, 74.56) * mm});
            skLineSegment(sketch, "E99.right", {"start": v(13.88, 75.32) * mm, "end": v(13.88, 74.56) * mm});
            skLineSegment(sketch, "E100.bottom", {"start": v(14, 75.32) * mm, "end": v(16.5, 75.32) * mm});
            skLineSegment(sketch, "E100.top", {"start": v(14, 74.56) * mm, "end": v(16.5, 74.56) * mm});
            skLineSegment(sketch, "E100.left", {"start": v(14, 75.32) * mm, "end": v(14, 74.56) * mm});
            skLineSegment(sketch, "E100.right", {"start": v(16.5, 75.32) * mm, "end": v(16.5, 74.56) * mm});
            skLineSegment(sketch, "E101.bottom", {"start": v(16.64, 75.32) * mm, "end": v(19.12, 75.32) * mm});
            skLineSegment(sketch, "E101.top", {"start": v(16.64, 74.56) * mm, "end": v(19.12, 74.56) * mm});
            skLineSegment(sketch, "E101.left", {"start": v(16.64, 75.32) * mm, "end": v(16.64, 74.56) * mm});
            skLineSegment(sketch, "E101.right", {"start": v(19.12, 75.32) * mm, "end": v(19.12, 74.56) * mm});
            skLineSegment(sketch, "E102.bottom", {"start": v(19.24, 75.32) * mm, "end": v(21.73, 75.32) * mm});
            skLineSegment(sketch, "E102.top", {"start": v(19.24, 74.56) * mm, "end": v(21.73, 74.56) * mm});
            skLineSegment(sketch, "E102.left", {"start": v(19.24, 75.32) * mm, "end": v(19.24, 74.56) * mm});
            skLineSegment(sketch, "E102.right", {"start": v(21.73, 75.32) * mm, "end": v(21.73, 74.56) * mm});
            skLineSegment(sketch, "E103.bottom", {"start": v(21.85, 75.32) * mm, "end": v(24.34, 75.32) * mm});
            skLineSegment(sketch, "E103.top", {"start": v(21.85, 74.56) * mm, "end": v(24.34, 74.56) * mm});
            skLineSegment(sketch, "E103.left", {"start": v(21.85, 75.32) * mm, "end": v(21.85, 74.56) * mm});
            skLineSegment(sketch, "E103.right", {"start": v(24.34, 75.32) * mm, "end": v(24.34, 74.56) * mm});
            skLineSegment(sketch, "E104.bottom", {"start": v(24.46, 75.32) * mm, "end": v(26.94, 75.32) * mm});
            skLineSegment(sketch, "E104.top", {"start": v(24.46, 74.56) * mm, "end": v(26.94, 74.56) * mm});
            skLineSegment(sketch, "E104.left", {"start": v(24.46, 75.32) * mm, "end": v(24.46, 74.56) * mm});
            skLineSegment(sketch, "E104.right", {"start": v(26.94, 75.32) * mm, "end": v(26.94, 74.56) * mm});
            skLineSegment(sketch, "E105.bottom", {"start": v(27.07, 75.32) * mm, "end": v(29.57, 75.32) * mm});
            skLineSegment(sketch, "E105.top", {"start": v(27.07, 74.56) * mm, "end": v(29.57, 74.56) * mm});
            skLineSegment(sketch, "E105.left", {"start": v(27.07, 75.32) * mm, "end": v(27.07, 74.56) * mm});
            skLineSegment(sketch, "E105.right", {"start": v(29.57, 75.32) * mm, "end": v(29.57, 74.56) * mm});
            skLineSegment(sketch, "E106.bottom", {"start": v(29.7, 75.32) * mm, "end": v(32.17, 75.32) * mm});
            skLineSegment(sketch, "E106.top", {"start": v(29.7, 74.56) * mm, "end": v(32.17, 74.56) * mm});
            skLineSegment(sketch, "E106.left", {"start": v(29.7, 75.32) * mm, "end": v(29.7, 74.56) * mm});
            skLineSegment(sketch, "E106.right", {"start": v(32.17, 75.32) * mm, "end": v(32.17, 74.56) * mm});
            skLineSegment(sketch, "E107.bottom", {"start": v(32.3, 75.32) * mm, "end": v(34.77, 75.32) * mm});
            skLineSegment(sketch, "E107.top", {"start": v(32.3, 74.56) * mm, "end": v(34.77, 74.56) * mm});
            skLineSegment(sketch, "E107.left", {"start": v(32.3, 75.32) * mm, "end": v(32.3, 74.56) * mm});
            skLineSegment(sketch, "E107.right", {"start": v(34.77, 75.32) * mm, "end": v(34.77, 74.56) * mm});
            skLineSegment(sketch, "E108.bottom", {"start": v(34.9, 75.32) * mm, "end": v(37.4, 75.32) * mm});
            skLineSegment(sketch, "E108.top", {"start": v(34.9, 74.56) * mm, "end": v(37.4, 74.56) * mm});
            skLineSegment(sketch, "E108.left", {"start": v(34.9, 75.32) * mm, "end": v(34.9, 74.56) * mm});
            skLineSegment(sketch, "E108.right", {"start": v(37.4, 75.32) * mm, "end": v(37.4, 74.56) * mm});
            skLineSegment(sketch, "E109.bottom", {"start": v(37.53, 75.32) * mm, "end": v(40.02, 75.32) * mm});
            skLineSegment(sketch, "E109.top", {"start": v(37.53, 74.56) * mm, "end": v(40.02, 74.56) * mm});
            skLineSegment(sketch, "E109.left", {"start": v(37.53, 75.32) * mm, "end": v(37.53, 74.56) * mm});
            skLineSegment(sketch, "E109.right", {"start": v(40.02, 75.32) * mm, "end": v(40.02, 74.56) * mm});
            skLineSegment(sketch, "E110.bottom", {"start": v(40.15, 75.32) * mm, "end": v(42.63, 75.32) * mm});
            skLineSegment(sketch, "E110.top", {"start": v(40.15, 74.56) * mm, "end": v(42.63, 74.56) * mm});
            skLineSegment(sketch, "E110.left", {"start": v(40.15, 75.32) * mm, "end": v(40.15, 74.56) * mm});
            skLineSegment(sketch, "E110.right", {"start": v(42.63, 75.32) * mm, "end": v(42.63, 74.56) * mm});
            skLineSegment(sketch, "E111.bottom", {"start": v(42.75, 75.32) * mm, "end": v(45.25, 75.32) * mm});
            skLineSegment(sketch, "E111.top", {"start": v(42.75, 74.56) * mm, "end": v(45.25, 74.56) * mm});
            skLineSegment(sketch, "E111.left", {"start": v(42.75, 75.32) * mm, "end": v(42.75, 74.56) * mm});
            skLineSegment(sketch, "E111.right", {"start": v(45.25, 75.32) * mm, "end": v(45.25, 74.56) * mm});
            skLineSegment(sketch, "E112.bottom", {"start": v(45.38, 75.32) * mm, "end": v(47.87, 75.32) * mm});
            skLineSegment(sketch, "E112.top", {"start": v(45.38, 74.56) * mm, "end": v(47.87, 74.56) * mm});
            skLineSegment(sketch, "E112.left", {"start": v(45.38, 75.32) * mm, "end": v(45.38, 74.56) * mm});
            skLineSegment(sketch, "E112.right", {"start": v(47.87, 75.32) * mm, "end": v(47.87, 74.56) * mm});
            skLineSegment(sketch, "E113.bottom", {"start": v(48, 75.32) * mm, "end": v(50.5, 75.32) * mm});
            skLineSegment(sketch, "E113.top", {"start": v(48, 74.56) * mm, "end": v(50.5, 74.56) * mm});
            skLineSegment(sketch, "E113.left", {"start": v(48, 75.32) * mm, "end": v(48, 74.56) * mm});
            skLineSegment(sketch, "E113.right", {"start": v(50.5, 75.32) * mm, "end": v(50.5, 74.56) * mm});
            skLineSegment(sketch, "E114.bottom", {"start": v(50.63, 75.32) * mm, "end": v(53.1, 75.32) * mm});
            skLineSegment(sketch, "E114.top", {"start": v(50.63, 74.56) * mm, "end": v(53.1, 74.56) * mm});
            skLineSegment(sketch, "E114.left", {"start": v(50.63, 75.32) * mm, "end": v(50.63, 74.56) * mm});
            skLineSegment(sketch, "E114.right", {"start": v(53.1, 75.32) * mm, "end": v(53.1, 74.56) * mm});
            skLineSegment(sketch, "E115.bottom", {"start": v(53.23, 75.32) * mm, "end": v(55.72, 75.32) * mm});
            skLineSegment(sketch, "E115.top", {"start": v(53.23, 74.56) * mm, "end": v(55.72, 74.56) * mm});
            skLineSegment(sketch, "E115.left", {"start": v(53.23, 75.32) * mm, "end": v(53.23, 74.56) * mm});
            skLineSegment(sketch, "E115.right", {"start": v(55.72, 75.32) * mm, "end": v(55.72, 74.56) * mm});
            skLineSegment(sketch, "E116.bottom", {"start": v(55.86, 75.32) * mm, "end": v(58.34, 75.32) * mm});
            skLineSegment(sketch, "E116.top", {"start": v(55.86, 74.56) * mm, "end": v(58.34, 74.56) * mm});
            skLineSegment(sketch, "E116.left", {"start": v(55.86, 75.32) * mm, "end": v(55.86, 74.56) * mm});
            skLineSegment(sketch, "E116.right", {"start": v(58.34, 75.32) * mm, "end": v(58.34, 74.56) * mm});
            skLineSegment(sketch, "E117.bottom", {"start": v(58.46, 75.32) * mm, "end": v(60.95, 75.32) * mm});
            skLineSegment(sketch, "E117.top", {"start": v(58.46, 74.56) * mm, "end": v(60.95, 74.56) * mm});
            skLineSegment(sketch, "E117.left", {"start": v(58.46, 75.32) * mm, "end": v(58.46, 74.56) * mm});
            skLineSegment(sketch, "E117.right", {"start": v(60.95, 75.32) * mm, "end": v(60.95, 74.56) * mm});
            skLineSegment(sketch, "E118.bottom", {"start": v(61.07, 75.32) * mm, "end": v(63.55, 75.32) * mm});
            skLineSegment(sketch, "E118.top", {"start": v(61.07, 74.56) * mm, "end": v(63.55, 74.56) * mm});
            skLineSegment(sketch, "E118.left", {"start": v(61.07, 75.32) * mm, "end": v(61.07, 74.56) * mm});
            skLineSegment(sketch, "E118.right", {"start": v(63.55, 75.32) * mm, "end": v(63.55, 74.56) * mm});
            skLineSegment(sketch, "E119.bottom", {"start": v(63.68, 75.32) * mm, "end": v(66.17, 75.32) * mm});
            skLineSegment(sketch, "E119.top", {"start": v(63.68, 74.56) * mm, "end": v(66.17, 74.56) * mm});
            skLineSegment(sketch, "E119.left", {"start": v(63.68, 75.32) * mm, "end": v(63.68, 74.56) * mm});
            skLineSegment(sketch, "E119.right", {"start": v(66.17, 75.32) * mm, "end": v(66.17, 74.56) * mm});
            skLineSegment(sketch, "E120.bottom", {"start": v(66.3, 75.32) * mm, "end": v(68.8, 75.32) * mm});
            skLineSegment(sketch, "E120.top", {"start": v(66.3, 74.56) * mm, "end": v(68.8, 74.56) * mm});
            skLineSegment(sketch, "E120.left", {"start": v(66.3, 75.32) * mm, "end": v(66.3, 74.56) * mm});
            skLineSegment(sketch, "E120.right", {"start": v(68.8, 75.32) * mm, "end": v(68.8, 74.56) * mm});
            skLineSegment(sketch, "E121.bottom", {"start": v(68.93, 75.32) * mm, "end": v(71.43, 75.32) * mm});
            skLineSegment(sketch, "E121.top", {"start": v(68.93, 74.56) * mm, "end": v(71.43, 74.56) * mm});
            skLineSegment(sketch, "E121.left", {"start": v(68.93, 75.32) * mm, "end": v(68.93, 74.56) * mm});
            skLineSegment(sketch, "E121.right", {"start": v(71.43, 75.32) * mm, "end": v(71.43, 74.56) * mm});
            skLineSegment(sketch, "E122.bottom", {"start": v(71.56, 75.32) * mm, "end": v(74.05, 75.32) * mm});
            skLineSegment(sketch, "E122.top", {"start": v(71.56, 74.56) * mm, "end": v(74.05, 74.56) * mm});
            skLineSegment(sketch, "E122.left", {"start": v(71.56, 75.32) * mm, "end": v(71.56, 74.56) * mm});
            skLineSegment(sketch, "E122.right", {"start": v(74.05, 75.32) * mm, "end": v(74.05, 74.56) * mm});
            skLineSegment(sketch, "E123.bottom", {"start": v(74.18, 75.32) * mm, "end": v(76.67, 75.32) * mm});
            skLineSegment(sketch, "E123.top", {"start": v(74.18, 74.56) * mm, "end": v(76.67, 74.56) * mm});
            skLineSegment(sketch, "E123.left", {"start": v(74.18, 75.32) * mm, "end": v(74.18, 74.56) * mm});
            skLineSegment(sketch, "E123.right", {"start": v(76.67, 75.32) * mm, "end": v(76.67, 74.56) * mm});
            skLineSegment(sketch, "E124.bottom", {"start": v(-76.2, 73.52) * mm, "end": v(-75.01, 73.52) * mm});
            skLineSegment(sketch, "E124.top", {"start": v(-76.2, 72.75) * mm, "end": v(-75.01, 72.75) * mm});
            skLineSegment(sketch, "E124.left", {"start": v(-76.2, 73.52) * mm, "end": v(-76.2, 72.75) * mm});
            skLineSegment(sketch, "E124.right", {"start": v(-75.01, 73.52) * mm, "end": v(-75.01, 72.75) * mm});
            skLineSegment(sketch, "E125.bottom", {"start": v(-74.88, 73.52) * mm, "end": v(-72.38, 73.52) * mm});
            skLineSegment(sketch, "E125.top", {"start": v(-74.88, 72.75) * mm, "end": v(-72.38, 72.75) * mm});
            skLineSegment(sketch, "E125.left", {"start": v(-74.88, 73.52) * mm, "end": v(-74.88, 72.75) * mm});
            skLineSegment(sketch, "E125.right", {"start": v(-72.38, 73.52) * mm, "end": v(-72.38, 72.75) * mm});
            skLineSegment(sketch, "E126.bottom", {"start": v(-72.26, 73.52) * mm, "end": v(-69.76, 73.52) * mm});
            skLineSegment(sketch, "E126.top", {"start": v(-72.26, 72.75) * mm, "end": v(-69.76, 72.75) * mm});
            skLineSegment(sketch, "E126.left", {"start": v(-72.26, 73.52) * mm, "end": v(-72.26, 72.75) * mm});
            skLineSegment(sketch, "E126.right", {"start": v(-69.76, 73.52) * mm, "end": v(-69.76, 72.75) * mm});
            skLineSegment(sketch, "E127.bottom", {"start": v(-69.65, 73.52) * mm, "end": v(-67.16, 73.52) * mm});
            skLineSegment(sketch, "E127.top", {"start": v(-69.65, 72.75) * mm, "end": v(-67.16, 72.75) * mm});
            skLineSegment(sketch, "E127.left", {"start": v(-69.65, 73.52) * mm, "end": v(-69.65, 72.75) * mm});
            skLineSegment(sketch, "E127.right", {"start": v(-67.16, 73.52) * mm, "end": v(-67.16, 72.75) * mm});
            skLineSegment(sketch, "E128.bottom", {"start": v(-76.2, 72.62) * mm, "end": v(-73.71, 72.62) * mm});
            skLineSegment(sketch, "E128.top", {"start": v(-76.2, 71.85) * mm, "end": v(-73.71, 71.85) * mm});
            skLineSegment(sketch, "E128.left", {"start": v(-76.2, 72.62) * mm, "end": v(-76.2, 71.85) * mm});
            skLineSegment(sketch, "E128.right", {"start": v(-73.71, 72.62) * mm, "end": v(-73.71, 71.85) * mm});
            skLineSegment(sketch, "E129.bottom", {"start": v(-76.2, 71.72) * mm, "end": v(-75.01, 71.72) * mm});
            skLineSegment(sketch, "E129.top", {"start": v(-76.2, 70.95) * mm, "end": v(-75.01, 70.95) * mm});
            skLineSegment(sketch, "E129.left", {"start": v(-76.2, 71.72) * mm, "end": v(-76.2, 70.95) * mm});
            skLineSegment(sketch, "E129.right", {"start": v(-75.01, 71.72) * mm, "end": v(-75.01, 70.95) * mm});
            skLineSegment(sketch, "E130.bottom", {"start": v(-76.2, 70.81) * mm, "end": v(-73.71, 70.81) * mm});
            skLineSegment(sketch, "E130.top", {"start": v(-76.2, 70.06) * mm, "end": v(-73.71, 70.06) * mm});
            skLineSegment(sketch, "E130.left", {"start": v(-76.2, 70.81) * mm, "end": v(-76.2, 70.06) * mm});
            skLineSegment(sketch, "E130.right", {"start": v(-73.71, 70.81) * mm, "end": v(-73.71, 70.06) * mm});
            skLineSegment(sketch, "E131.bottom", {"start": v(-76.2, 69.93) * mm, "end": v(-75.01, 69.93) * mm});
            skLineSegment(sketch, "E131.top", {"start": v(-76.2, 69.16) * mm, "end": v(-75.01, 69.16) * mm});
            skLineSegment(sketch, "E131.left", {"start": v(-76.2, 69.93) * mm, "end": v(-76.2, 69.16) * mm});
            skLineSegment(sketch, "E131.right", {"start": v(-75.01, 69.93) * mm, "end": v(-75.01, 69.16) * mm});
            skLineSegment(sketch, "E132.bottom", {"start": v(-76.2, 69.03) * mm, "end": v(-73.71, 69.03) * mm});
            skLineSegment(sketch, "E132.top", {"start": v(-76.2, 68.27) * mm, "end": v(-73.71, 68.27) * mm});
            skLineSegment(sketch, "E132.left", {"start": v(-76.2, 69.03) * mm, "end": v(-76.2, 68.27) * mm});
            skLineSegment(sketch, "E132.right", {"start": v(-73.71, 69.03) * mm, "end": v(-73.71, 68.27) * mm});
            skLineSegment(sketch, "E133.bottom", {"start": v(-76.2, 68.13) * mm, "end": v(-75.01, 68.13) * mm});
            skLineSegment(sketch, "E133.top", {"start": v(-76.2, 67.37) * mm, "end": v(-75.01, 67.37) * mm});
            skLineSegment(sketch, "E133.left", {"start": v(-76.2, 68.13) * mm, "end": v(-76.2, 67.37) * mm});
            skLineSegment(sketch, "E133.right", {"start": v(-75.01, 68.13) * mm, "end": v(-75.01, 67.37) * mm});
            skLineSegment(sketch, "E134.bottom", {"start": v(-76.2, 67.24) * mm, "end": v(-73.71, 67.24) * mm});
            skLineSegment(sketch, "E134.top", {"start": v(-76.2, 66.47) * mm, "end": v(-73.71, 66.47) * mm});
            skLineSegment(sketch, "E134.left", {"start": v(-76.2, 67.24) * mm, "end": v(-76.2, 66.47) * mm});
            skLineSegment(sketch, "E134.right", {"start": v(-73.71, 67.24) * mm, "end": v(-73.71, 66.47) * mm});
            skLineSegment(sketch, "E135.bottom", {"start": v(-73.58, 72.62) * mm, "end": v(-71.1, 72.62) * mm});
            skLineSegment(sketch, "E135.top", {"start": v(-73.58, 71.85) * mm, "end": v(-71.1, 71.85) * mm});
            skLineSegment(sketch, "E135.left", {"start": v(-73.58, 72.62) * mm, "end": v(-73.58, 71.85) * mm});
            skLineSegment(sketch, "E135.right", {"start": v(-71.1, 72.62) * mm, "end": v(-71.1, 71.85) * mm});
            skLineSegment(sketch, "E136.bottom", {"start": v(-70.99, 72.62) * mm, "end": v(-68.49, 72.62) * mm});
            skLineSegment(sketch, "E136.top", {"start": v(-70.99, 71.85) * mm, "end": v(-68.49, 71.85) * mm});
            skLineSegment(sketch, "E136.left", {"start": v(-70.99, 72.62) * mm, "end": v(-70.99, 71.85) * mm});
            skLineSegment(sketch, "E136.right", {"start": v(-68.49, 72.62) * mm, "end": v(-68.49, 71.85) * mm});
            skLineSegment(sketch, "E137.bottom", {"start": v(-68.35, 72.62) * mm, "end": v(-65.86, 72.62) * mm});
            skLineSegment(sketch, "E137.top", {"start": v(-68.35, 71.85) * mm, "end": v(-65.86, 71.85) * mm});
            skLineSegment(sketch, "E137.left", {"start": v(-68.35, 72.62) * mm, "end": v(-68.35, 71.85) * mm});
            skLineSegment(sketch, "E137.right", {"start": v(-65.86, 72.62) * mm, "end": v(-65.86, 71.85) * mm});
            skLineSegment(sketch, "E138.bottom", {"start": v(-74.88, 71.72) * mm, "end": v(-72.38, 71.72) * mm});
            skLineSegment(sketch, "E138.top", {"start": v(-74.88, 70.95) * mm, "end": v(-72.38, 70.95) * mm});
            skLineSegment(sketch, "E138.left", {"start": v(-74.88, 71.72) * mm, "end": v(-74.88, 70.95) * mm});
            skLineSegment(sketch, "E138.right", {"start": v(-72.38, 71.72) * mm, "end": v(-72.38, 70.95) * mm});
            skLineSegment(sketch, "E139.bottom", {"start": v(-72.26, 71.72) * mm, "end": v(-69.76, 71.72) * mm});
            skLineSegment(sketch, "E139.top", {"start": v(-72.26, 70.95) * mm, "end": v(-69.76, 70.95) * mm});
            skLineSegment(sketch, "E139.left", {"start": v(-72.26, 71.72) * mm, "end": v(-72.26, 70.95) * mm});
            skLineSegment(sketch, "E139.right", {"start": v(-69.76, 71.72) * mm, "end": v(-69.76, 70.95) * mm});
            skLineSegment(sketch, "E140.bottom", {"start": v(-69.65, 71.72) * mm, "end": v(-67.16, 71.72) * mm});
            skLineSegment(sketch, "E140.top", {"start": v(-69.65, 70.95) * mm, "end": v(-67.16, 70.95) * mm});
            skLineSegment(sketch, "E140.left", {"start": v(-69.65, 71.72) * mm, "end": v(-69.65, 70.95) * mm});
            skLineSegment(sketch, "E140.right", {"start": v(-67.16, 71.72) * mm, "end": v(-67.16, 70.95) * mm});
            skLineSegment(sketch, "E141.bottom", {"start": v(-73.58, 70.81) * mm, "end": v(-71.1, 70.81) * mm});
            skLineSegment(sketch, "E141.top", {"start": v(-73.58, 70.06) * mm, "end": v(-71.1, 70.06) * mm});
            skLineSegment(sketch, "E141.left", {"start": v(-73.58, 70.81) * mm, "end": v(-73.58, 70.06) * mm});
            skLineSegment(sketch, "E141.right", {"start": v(-71.1, 70.81) * mm, "end": v(-71.1, 70.06) * mm});
            skLineSegment(sketch, "E142.bottom", {"start": v(-74.88, 69.93) * mm, "end": v(-72.38, 69.93) * mm});
            skLineSegment(sketch, "E142.top", {"start": v(-74.88, 69.16) * mm, "end": v(-72.38, 69.16) * mm});
            skLineSegment(sketch, "E142.left", {"start": v(-74.88, 69.93) * mm, "end": v(-74.88, 69.16) * mm});
            skLineSegment(sketch, "E142.right", {"start": v(-72.38, 69.93) * mm, "end": v(-72.38, 69.16) * mm});
            skLineSegment(sketch, "E143.bottom", {"start": v(-70.99, 70.81) * mm, "end": v(-68.49, 70.81) * mm});
            skLineSegment(sketch, "E143.top", {"start": v(-70.99, 70.06) * mm, "end": v(-68.49, 70.06) * mm});
            skLineSegment(sketch, "E143.left", {"start": v(-70.99, 70.81) * mm, "end": v(-70.99, 70.06) * mm});
            skLineSegment(sketch, "E143.right", {"start": v(-68.49, 70.81) * mm, "end": v(-68.49, 70.06) * mm});
            skLineSegment(sketch, "E144.bottom", {"start": v(-72.26, 69.93) * mm, "end": v(-69.76, 69.93) * mm});
            skLineSegment(sketch, "E144.top", {"start": v(-72.26, 69.16) * mm, "end": v(-69.76, 69.16) * mm});
            skLineSegment(sketch, "E144.left", {"start": v(-72.26, 69.93) * mm, "end": v(-72.26, 69.16) * mm});
            skLineSegment(sketch, "E144.right", {"start": v(-69.76, 69.93) * mm, "end": v(-69.76, 69.16) * mm});
            skLineSegment(sketch, "E145.bottom", {"start": v(-73.58, 69.03) * mm, "end": v(-71.1, 69.03) * mm});
            skLineSegment(sketch, "E145.top", {"start": v(-73.58, 68.27) * mm, "end": v(-71.1, 68.27) * mm});
            skLineSegment(sketch, "E145.left", {"start": v(-73.58, 69.03) * mm, "end": v(-73.58, 68.27) * mm});
            skLineSegment(sketch, "E145.right", {"start": v(-71.1, 69.03) * mm, "end": v(-71.1, 68.27) * mm});
            skLineSegment(sketch, "E146.bottom", {"start": v(-65.72, 74.43) * mm, "end": v(-63.23, 74.43) * mm});
            skLineSegment(sketch, "E146.top", {"start": v(-65.72, 73.65) * mm, "end": v(-63.23, 73.65) * mm});
            skLineSegment(sketch, "E146.left", {"start": v(-65.72, 74.43) * mm, "end": v(-65.72, 73.65) * mm});
            skLineSegment(sketch, "E146.right", {"start": v(-63.23, 74.43) * mm, "end": v(-63.23, 73.65) * mm});
            skLineSegment(sketch, "E147.bottom", {"start": v(-63.1, 74.43) * mm, "end": v(-60.62, 74.43) * mm});
            skLineSegment(sketch, "E147.top", {"start": v(-63.1, 73.65) * mm, "end": v(-60.62, 73.65) * mm});
            skLineSegment(sketch, "E147.left", {"start": v(-63.1, 74.43) * mm, "end": v(-63.1, 73.65) * mm});
            skLineSegment(sketch, "E147.right", {"start": v(-60.62, 74.43) * mm, "end": v(-60.62, 73.65) * mm});
            skLineSegment(sketch, "E148.bottom", {"start": v(-60.5, 74.43) * mm, "end": v(-58.02, 74.43) * mm});
            skLineSegment(sketch, "E148.top", {"start": v(-60.5, 73.65) * mm, "end": v(-58.02, 73.65) * mm});
            skLineSegment(sketch, "E148.left", {"start": v(-60.5, 74.43) * mm, "end": v(-60.5, 73.65) * mm});
            skLineSegment(sketch, "E148.right", {"start": v(-58.02, 74.43) * mm, "end": v(-58.02, 73.65) * mm});
            skLineSegment(sketch, "E149.bottom", {"start": v(-57.9, 74.43) * mm, "end": v(-55.4, 74.43) * mm});
            skLineSegment(sketch, "E149.top", {"start": v(-57.9, 73.65) * mm, "end": v(-55.4, 73.65) * mm});
            skLineSegment(sketch, "E149.left", {"start": v(-57.9, 74.43) * mm, "end": v(-57.9, 73.65) * mm});
            skLineSegment(sketch, "E149.right", {"start": v(-55.4, 74.43) * mm, "end": v(-55.4, 73.65) * mm});
            skLineSegment(sketch, "E150.bottom", {"start": v(-55.27, 74.43) * mm, "end": v(-52.78, 74.43) * mm});
            skLineSegment(sketch, "E150.top", {"start": v(-55.27, 73.65) * mm, "end": v(-52.78, 73.65) * mm});
            skLineSegment(sketch, "E150.left", {"start": v(-55.27, 74.43) * mm, "end": v(-55.27, 73.65) * mm});
            skLineSegment(sketch, "E150.right", {"start": v(-52.78, 74.43) * mm, "end": v(-52.78, 73.65) * mm});
            skLineSegment(sketch, "E151.bottom", {"start": v(-52.66, 74.43) * mm, "end": v(-50.18, 74.43) * mm});
            skLineSegment(sketch, "E151.top", {"start": v(-52.66, 73.65) * mm, "end": v(-50.18, 73.65) * mm});
            skLineSegment(sketch, "E151.left", {"start": v(-52.66, 74.43) * mm, "end": v(-52.66, 73.65) * mm});
            skLineSegment(sketch, "E151.right", {"start": v(-50.18, 74.43) * mm, "end": v(-50.18, 73.65) * mm});
            skLineSegment(sketch, "E152.bottom", {"start": v(-67.04, 73.52) * mm, "end": v(-64.55, 73.52) * mm});
            skLineSegment(sketch, "E152.top", {"start": v(-67.04, 72.75) * mm, "end": v(-64.55, 72.75) * mm});
            skLineSegment(sketch, "E152.left", {"start": v(-67.04, 73.52) * mm, "end": v(-67.04, 72.75) * mm});
            skLineSegment(sketch, "E152.right", {"start": v(-64.55, 73.52) * mm, "end": v(-64.55, 72.75) * mm});
            skLineSegment(sketch, "E153.bottom", {"start": v(-64.42, 73.52) * mm, "end": v(-61.95, 73.52) * mm});
            skLineSegment(sketch, "E153.top", {"start": v(-64.42, 72.75) * mm, "end": v(-61.95, 72.75) * mm});
            skLineSegment(sketch, "E153.left", {"start": v(-64.42, 73.52) * mm, "end": v(-64.42, 72.75) * mm});
            skLineSegment(sketch, "E153.right", {"start": v(-61.95, 73.52) * mm, "end": v(-61.95, 72.75) * mm});
            skLineSegment(sketch, "E154.bottom", {"start": v(-50.06, 74.43) * mm, "end": v(-47.57, 74.43) * mm});
            skLineSegment(sketch, "E154.top", {"start": v(-50.06, 73.65) * mm, "end": v(-47.57, 73.65) * mm});
            skLineSegment(sketch, "E154.left", {"start": v(-50.06, 74.43) * mm, "end": v(-50.06, 73.65) * mm});
            skLineSegment(sketch, "E154.right", {"start": v(-47.57, 74.43) * mm, "end": v(-47.57, 73.65) * mm});
            skLineSegment(sketch, "E155.bottom", {"start": v(-61.83, 73.52) * mm, "end": v(-59.35, 73.52) * mm});
            skLineSegment(sketch, "E155.top", {"start": v(-61.83, 72.75) * mm, "end": v(-59.35, 72.75) * mm});
            skLineSegment(sketch, "E155.left", {"start": v(-61.83, 73.52) * mm, "end": v(-61.83, 72.75) * mm});
            skLineSegment(sketch, "E155.right", {"start": v(-59.35, 73.52) * mm, "end": v(-59.35, 72.75) * mm});
            skLineSegment(sketch, "E156.bottom", {"start": v(-59.22, 73.52) * mm, "end": v(-56.74, 73.52) * mm});
            skLineSegment(sketch, "E156.top", {"start": v(-59.22, 72.75) * mm, "end": v(-56.74, 72.75) * mm});
            skLineSegment(sketch, "E156.left", {"start": v(-59.22, 73.52) * mm, "end": v(-59.22, 72.75) * mm});
            skLineSegment(sketch, "E156.right", {"start": v(-56.74, 73.52) * mm, "end": v(-56.74, 72.75) * mm});
            skLineSegment(sketch, "E157.bottom", {"start": v(-65.72, 72.62) * mm, "end": v(-63.23, 72.62) * mm});
            skLineSegment(sketch, "E157.top", {"start": v(-65.72, 71.85) * mm, "end": v(-63.23, 71.85) * mm});
            skLineSegment(sketch, "E157.left", {"start": v(-65.72, 72.62) * mm, "end": v(-65.72, 71.85) * mm});
            skLineSegment(sketch, "E157.right", {"start": v(-63.23, 72.62) * mm, "end": v(-63.23, 71.85) * mm});
            skLineSegment(sketch, "E158.bottom", {"start": v(-67.04, 71.72) * mm, "end": v(-64.55, 71.72) * mm});
            skLineSegment(sketch, "E158.top", {"start": v(-67.04, 70.95) * mm, "end": v(-64.55, 70.95) * mm});
            skLineSegment(sketch, "E158.left", {"start": v(-67.04, 71.72) * mm, "end": v(-67.04, 70.95) * mm});
            skLineSegment(sketch, "E158.right", {"start": v(-64.55, 71.72) * mm, "end": v(-64.55, 70.95) * mm});
            skLineSegment(sketch, "E159.bottom", {"start": v(-68.35, 70.81) * mm, "end": v(-65.86, 70.81) * mm});
            skLineSegment(sketch, "E159.top", {"start": v(-68.35, 70.06) * mm, "end": v(-65.86, 70.06) * mm});
            skLineSegment(sketch, "E159.left", {"start": v(-68.35, 70.81) * mm, "end": v(-68.35, 70.06) * mm});
            skLineSegment(sketch, "E159.right", {"start": v(-65.86, 70.81) * mm, "end": v(-65.86, 70.06) * mm});
            skLineSegment(sketch, "E160.bottom", {"start": v(-65.72, 70.81) * mm, "end": v(-63.23, 70.81) * mm});
            skLineSegment(sketch, "E160.top", {"start": v(-65.72, 70.06) * mm, "end": v(-63.23, 70.06) * mm});
            skLineSegment(sketch, "E160.left", {"start": v(-65.72, 70.81) * mm, "end": v(-65.72, 70.06) * mm});
            skLineSegment(sketch, "E160.right", {"start": v(-63.23, 70.81) * mm, "end": v(-63.23, 70.06) * mm});
            skLineSegment(sketch, "E161.bottom", {"start": v(-63.1, 72.62) * mm, "end": v(-60.62, 72.62) * mm});
            skLineSegment(sketch, "E161.top", {"start": v(-63.1, 71.85) * mm, "end": v(-60.62, 71.85) * mm});
            skLineSegment(sketch, "E161.left", {"start": v(-63.1, 72.62) * mm, "end": v(-63.1, 71.85) * mm});
            skLineSegment(sketch, "E161.right", {"start": v(-60.62, 72.62) * mm, "end": v(-60.62, 71.85) * mm});
            skLineSegment(sketch, "E162.bottom", {"start": v(-64.42, 71.72) * mm, "end": v(-61.95, 71.72) * mm});
            skLineSegment(sketch, "E162.top", {"start": v(-64.42, 70.95) * mm, "end": v(-61.95, 70.95) * mm});
            skLineSegment(sketch, "E162.left", {"start": v(-64.42, 71.72) * mm, "end": v(-64.42, 70.95) * mm});
            skLineSegment(sketch, "E162.right", {"start": v(-61.95, 71.72) * mm, "end": v(-61.95, 70.95) * mm});
            skLineSegment(sketch, "E163.bottom", {"start": v(-63.1, 70.81) * mm, "end": v(-60.62, 70.81) * mm});
            skLineSegment(sketch, "E163.top", {"start": v(-63.1, 70.06) * mm, "end": v(-60.62, 70.06) * mm});
            skLineSegment(sketch, "E163.left", {"start": v(-63.1, 70.81) * mm, "end": v(-63.1, 70.06) * mm});
            skLineSegment(sketch, "E163.right", {"start": v(-60.62, 70.81) * mm, "end": v(-60.62, 70.06) * mm});
            skLineSegment(sketch, "E164.bottom", {"start": v(-61.83, 71.72) * mm, "end": v(-59.35, 71.72) * mm});
            skLineSegment(sketch, "E164.top", {"start": v(-61.83, 70.95) * mm, "end": v(-59.35, 70.95) * mm});
            skLineSegment(sketch, "E164.left", {"start": v(-61.83, 71.72) * mm, "end": v(-61.83, 70.95) * mm});
            skLineSegment(sketch, "E164.right", {"start": v(-59.35, 71.72) * mm, "end": v(-59.35, 70.95) * mm});
            skLineSegment(sketch, "E165.bottom", {"start": v(-60.5, 72.62) * mm, "end": v(-58.02, 72.62) * mm});
            skLineSegment(sketch, "E165.top", {"start": v(-60.5, 71.85) * mm, "end": v(-58.02, 71.85) * mm});
            skLineSegment(sketch, "E165.left", {"start": v(-60.5, 72.62) * mm, "end": v(-60.5, 71.85) * mm});
            skLineSegment(sketch, "E165.right", {"start": v(-58.02, 72.62) * mm, "end": v(-58.02, 71.85) * mm});
            skLineSegment(sketch, "E166.bottom", {"start": v(-60.5, 70.81) * mm, "end": v(-58.02, 70.81) * mm});
            skLineSegment(sketch, "E166.top", {"start": v(-60.5, 70.06) * mm, "end": v(-58.02, 70.06) * mm});
            skLineSegment(sketch, "E166.left", {"start": v(-60.5, 70.81) * mm, "end": v(-60.5, 70.06) * mm});
            skLineSegment(sketch, "E166.right", {"start": v(-58.02, 70.81) * mm, "end": v(-58.02, 70.06) * mm});
            skLineSegment(sketch, "E167.bottom", {"start": v(-59.22, 71.72) * mm, "end": v(-56.74, 71.72) * mm});
            skLineSegment(sketch, "E167.top", {"start": v(-59.22, 70.95) * mm, "end": v(-56.74, 70.95) * mm});
            skLineSegment(sketch, "E167.left", {"start": v(-59.22, 71.72) * mm, "end": v(-59.22, 70.95) * mm});
            skLineSegment(sketch, "E167.right", {"start": v(-56.74, 71.72) * mm, "end": v(-56.74, 70.95) * mm});
            skLineSegment(sketch, "E168.bottom", {"start": v(-57.9, 72.62) * mm, "end": v(-55.4, 72.62) * mm});
            skLineSegment(sketch, "E168.top", {"start": v(-57.9, 71.85) * mm, "end": v(-55.4, 71.85) * mm});
            skLineSegment(sketch, "E168.left", {"start": v(-57.9, 72.62) * mm, "end": v(-57.9, 71.85) * mm});
            skLineSegment(sketch, "E168.right", {"start": v(-55.4, 72.62) * mm, "end": v(-55.4, 71.85) * mm});
            skLineSegment(sketch, "E169.bottom", {"start": v(-56.61, 73.52) * mm, "end": v(-54.13, 73.52) * mm});
            skLineSegment(sketch, "E169.top", {"start": v(-56.61, 72.75) * mm, "end": v(-54.13, 72.75) * mm});
            skLineSegment(sketch, "E169.left", {"start": v(-56.61, 73.52) * mm, "end": v(-56.61, 72.75) * mm});
            skLineSegment(sketch, "E169.right", {"start": v(-54.13, 73.52) * mm, "end": v(-54.13, 72.75) * mm});
            skLineSegment(sketch, "E170.bottom", {"start": v(-57.9, 70.81) * mm, "end": v(-55.4, 70.81) * mm});
            skLineSegment(sketch, "E170.top", {"start": v(-57.9, 70.06) * mm, "end": v(-55.4, 70.06) * mm});
            skLineSegment(sketch, "E170.left", {"start": v(-57.9, 70.81) * mm, "end": v(-57.9, 70.06) * mm});
            skLineSegment(sketch, "E170.right", {"start": v(-55.4, 70.81) * mm, "end": v(-55.4, 70.06) * mm});
            skLineSegment(sketch, "E171.bottom", {"start": v(-56.61, 71.72) * mm, "end": v(-54.13, 71.72) * mm});
            skLineSegment(sketch, "E171.top", {"start": v(-56.61, 70.95) * mm, "end": v(-54.13, 70.95) * mm});
            skLineSegment(sketch, "E171.left", {"start": v(-56.61, 71.72) * mm, "end": v(-56.61, 70.95) * mm});
            skLineSegment(sketch, "E171.right", {"start": v(-54.13, 71.72) * mm, "end": v(-54.13, 70.95) * mm});
            skLineSegment(sketch, "E172.bottom", {"start": v(-55.27, 72.62) * mm, "end": v(-52.78, 72.62) * mm});
            skLineSegment(sketch, "E172.top", {"start": v(-55.27, 71.85) * mm, "end": v(-52.78, 71.85) * mm});
            skLineSegment(sketch, "E172.left", {"start": v(-55.27, 72.62) * mm, "end": v(-55.27, 71.85) * mm});
            skLineSegment(sketch, "E172.right", {"start": v(-52.78, 72.62) * mm, "end": v(-52.78, 71.85) * mm});
            skSolve(sketch);
        }
        {
            var Q0;
            Q0 = qSketchRegion(id + "F2", true);
            extrude(context, id + "F3", {"entities" : qUnion([Q0]), "operationType" : NewBodyOperationType.ADD, "depth" : 0.25 * mm, "offsetDistance" : 25.4 * mm});
        }
    });
